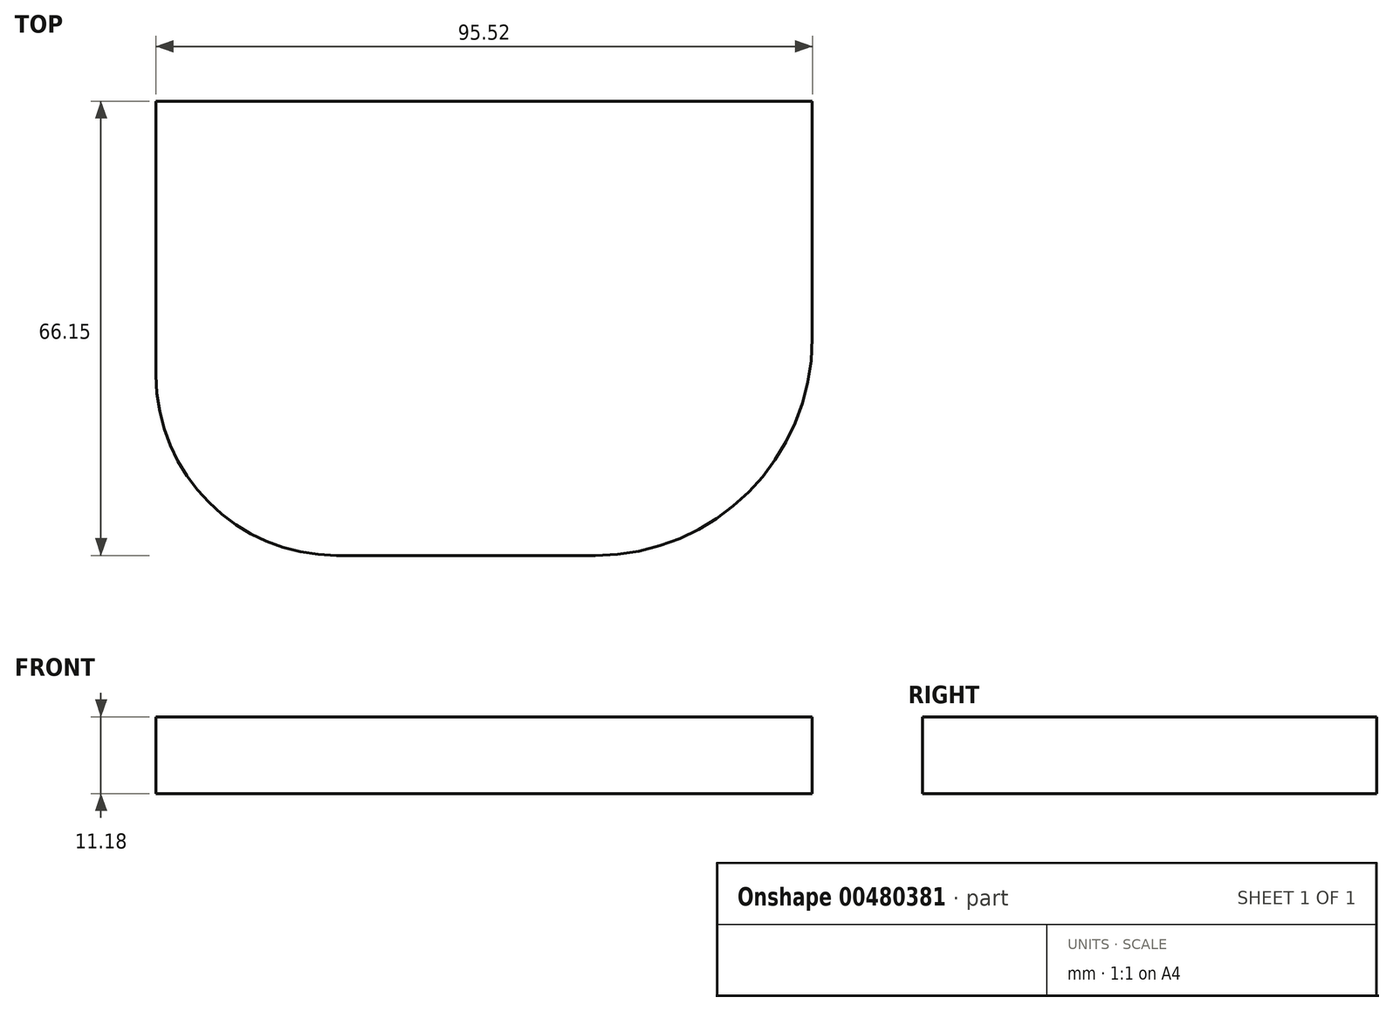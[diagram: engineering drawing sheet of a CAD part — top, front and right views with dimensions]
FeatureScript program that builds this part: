
annotation { "Feature Type Name" : "Feature", "Feature Type Description" : "" }
export const myFeature = defineFeature(function(context is Context, id is Id, definition is map)
    precondition{}
    {
        {
            var Q0;
            Q0=qCreatedBy(makeId("Top.planeOp"),FACE);
            var sketch = newSketch(context, id + "F0", { "sketchPlane" : qUnion([Q0])});
            skLineSegment(sketch, "E0.bottom", {"start": v(-47.76, 39.87) * mm, "end": v(47.76, 39.87) * mm});
            skLineSegment(sketch, "E0.top", {"start": v(-21.47, -39.87) * mm, "end": v(16.16, -39.87) * mm});
            skLineSegment(sketch, "E0.left", {"start": v(-47.76, 39.87) * mm, "end": v(-47.76, -13.58) * mm});
            skLineSegment(sketch, "E0.right", {"start": v(47.76, 39.87) * mm, "end": v(47.76, -8.27) * mm});
            skPoint(sketch, "E0.middle", {"position": v(0, 0) * mm});
            skPoint(sketch, "E1.visualSharp", {"position": v(47.76, -39.87) * mm});
            skArc(sketch, "E1.filletArc", {"start": v(16.16, -39.87) * mm, "mid": v(38.5, -30.61) * mm, "end": v(47.76, -8.27) * mm});
            skPoint(sketch, "E2.visualSharp", {"position": v(-47.76, -39.87) * mm});
            skArc(sketch, "E2.filletArc", {"start": v(-47.76, -13.58) * mm, "mid": v(-40.06, -32.17) * mm, "end": v(-21.47, -39.87) * mm});
            skLineSegment(sketch, "E3.bottom", {"start": v(47.76, 39.87) * mm, "end": v(-47.76, 39.87) * mm});
            skLineSegment(sketch, "E3.top", {"start": v(47.76, 26.28) * mm, "end": v(-47.76, 26.28) * mm});
            skLineSegment(sketch, "E3.left", {"start": v(47.76, 39.87) * mm, "end": v(47.76, 26.28) * mm});
            skLineSegment(sketch, "E3.right", {"start": v(-47.76, 39.87) * mm, "end": v(-47.76, 26.28) * mm});
            skSolve(sketch);
        }
        {
            var Q0;
            Q0=makeQuery(id+"F0.imprint","IMPRINT",FACE,{"disambiguationData":[TD([[makeQuery(id+"F0.imprint","IMPRINT",EDGE,{"derivedFrom":sQuery(id+"F0.wireOp",EDGE,"E0.top")}),1.0]])]});
            extrude(context, id + "F1", {"entities" : qUnion([Q0]), "depth" : 11.18 * mm});
        }
    });
